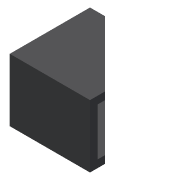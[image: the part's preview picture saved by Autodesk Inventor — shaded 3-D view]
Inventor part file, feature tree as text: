
AUTODESK INVENTOR PART (.ipt)
format: ipt  version: 2014 (Build 180170000, 170)  size: 83,456 bytes
history: native  units: mm
features: extrude x2, sketch x2
ambient origin geometry x8: Origin, YZ Plane, XZ Plane, XY Plane, X Axis, Y Axis, Z Axis, Center Point
bodies: Solid1 (feature_tree)
feature tree (4):
  extrude  "Extrusion1"  Depth=32.0mm
  extrude  "Extrusion2"  Depth=3.0mm
  sketch  "Sketch1"  dims[d0=32.0mm d1=6.0mm]
  sketch  "Sketch2"  dims[d2=25.0mm d3=0.0mm d4=3.0mm d5=3.0mm d6=3.0mm d7=29.0mm d8=0.0mm]
